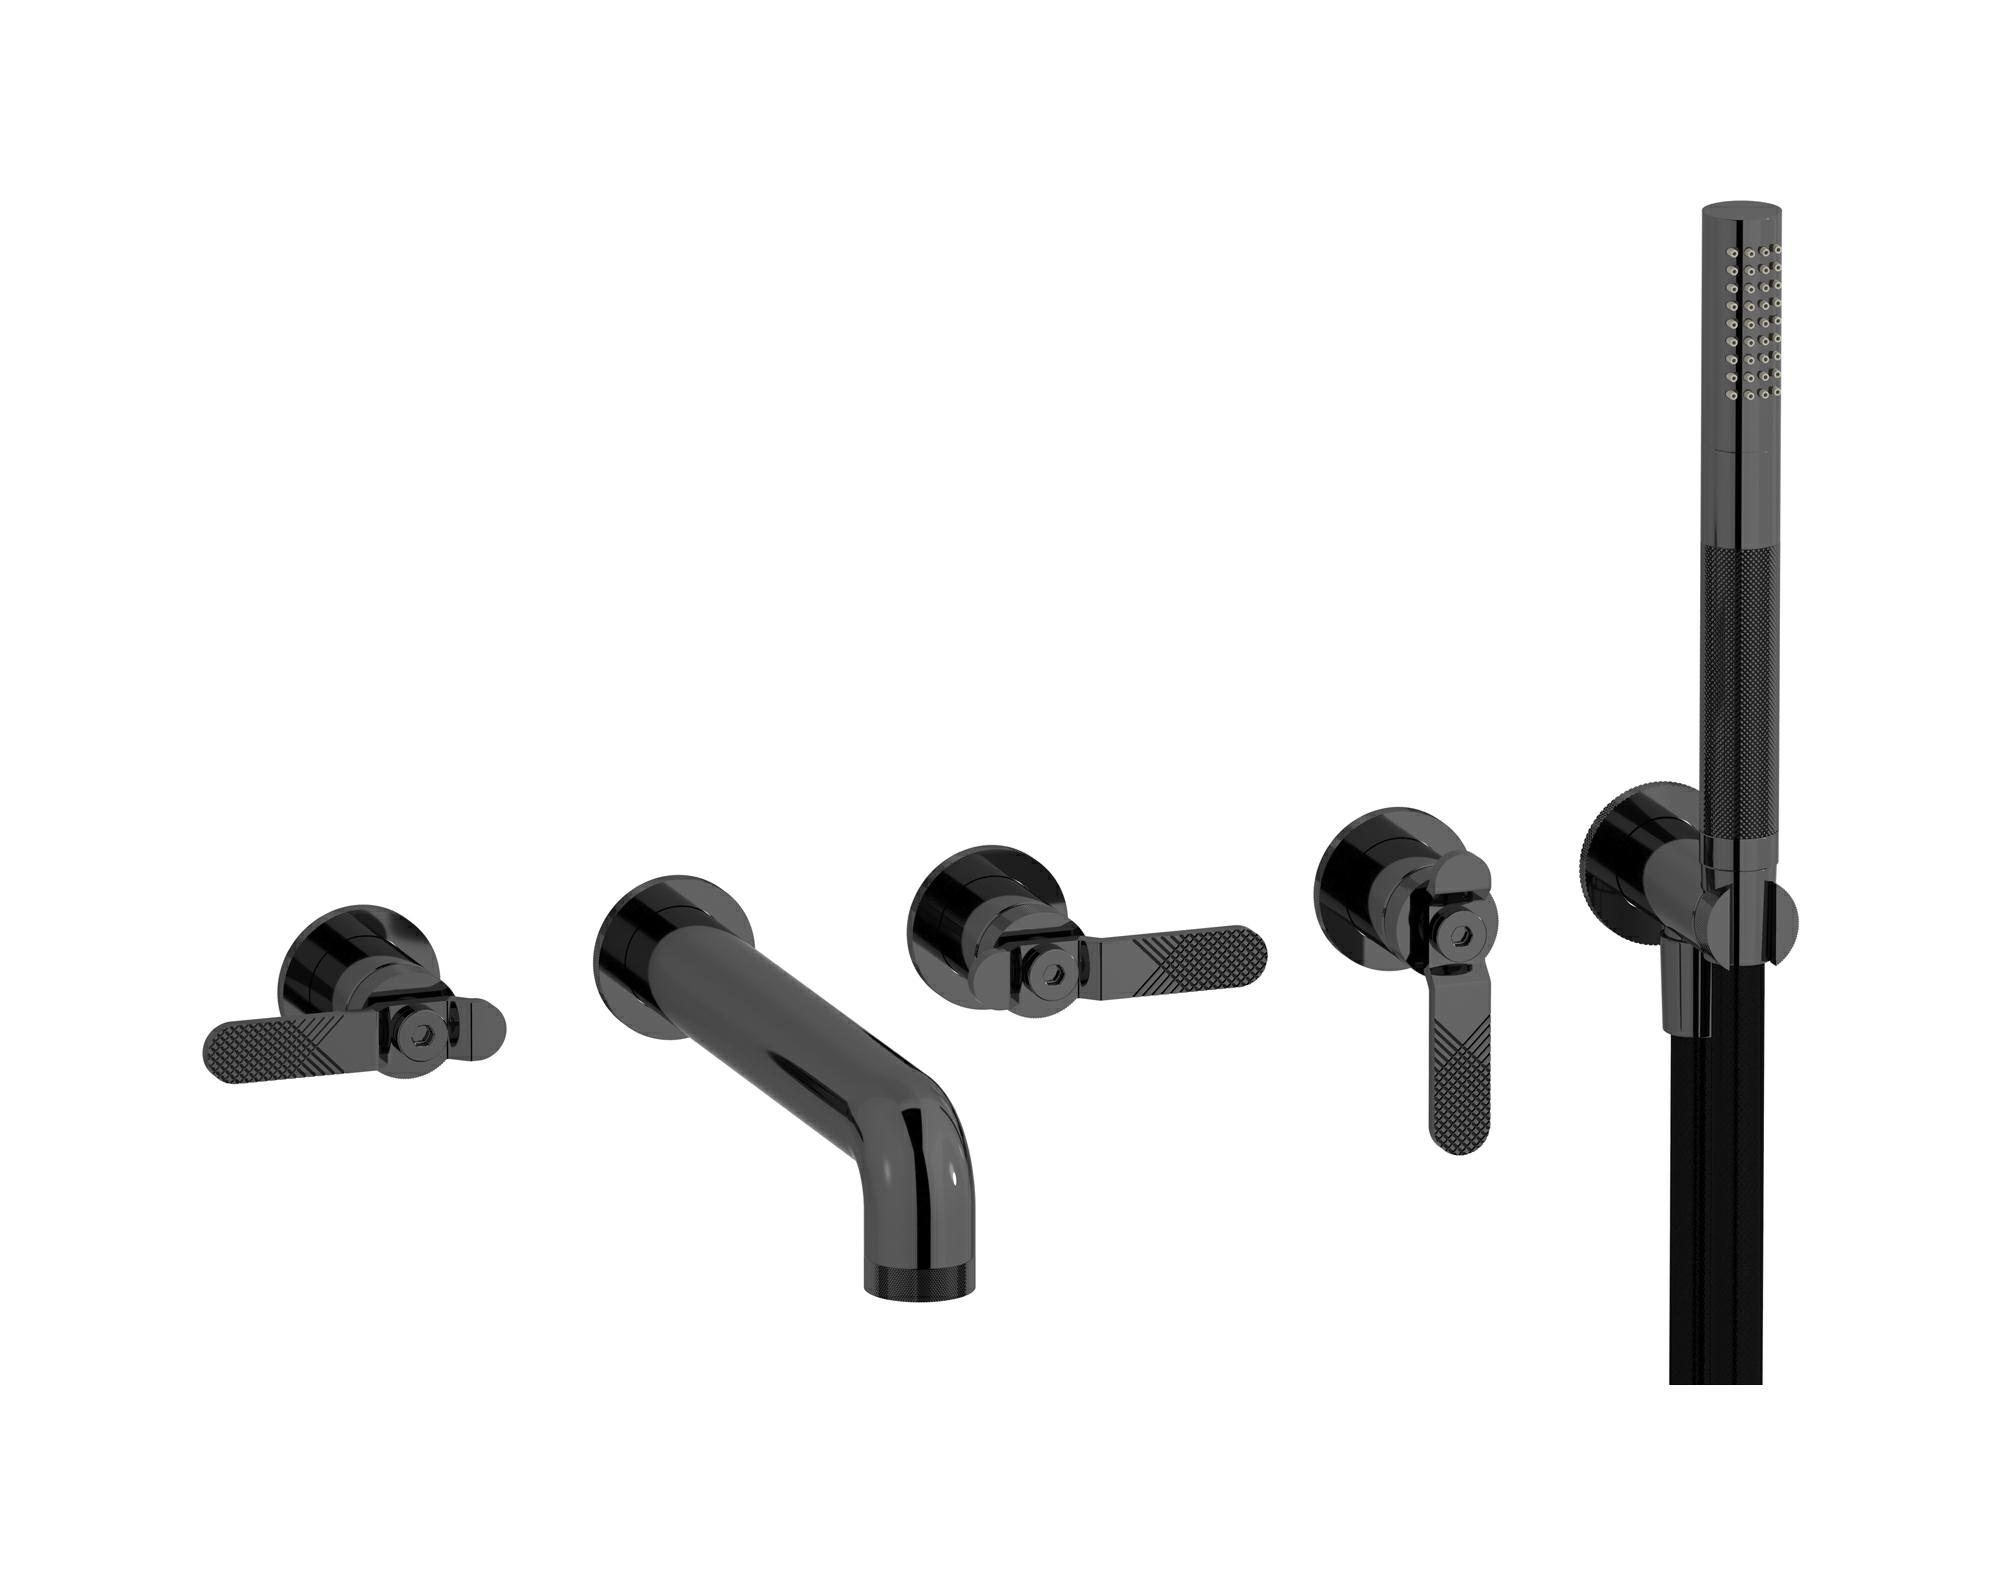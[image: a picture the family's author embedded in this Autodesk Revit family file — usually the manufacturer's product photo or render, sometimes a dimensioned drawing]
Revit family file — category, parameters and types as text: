
# Revit family: B2398
name_source: partatom
category: Apparecchi idraulici
units: mm (PartAtom-declared; Revit-internal decimal feet)

## family parameters
Basato su piano di lavoro = No
Condiviso = No
Mantieni orientamento annotazione = No
Numero OmniClass = 23.45.55.17
Punto di calcolo locali = No
Quota connettore circolare = Usa diametro
Sempre verticale = Sì
Taglio con vuoti quando caricato = No
Tipo di parte = Normale
Titolo OmniClass = Mixing Faucets

## types (13) — shared parameters
Cold water inlet = 10 mm  [stored 0.0328084 ft]
Commenti sul tipo = Five holes wall mounted bath filler with shower kit
Connessione CW = No
Connessione HW = No
Connessione di scarico = No
Connessione di ventilazione = No
Descrizione = Five holes wall mounted bath filler with shower kit
Hot water inlet = 10 mm  [stored 0.0328084 ft]
Produttore = IB Rubinetterie S.p.A.
URL = https://www.weareib.it
zero-valued in all types: Prospetto di default

## per-type parameters (varying)
| type | Finishes surface | Immagine tipo | Modello |
| Chrome | IB_Chrome | B2398CC.jpg | B2398CC |
| Black Chrome | IB_Black chrome | B2398CF.jpg | B2398CF |
| Brushed Black Chrome | IB_Brushed black chrome | B2398CS.jpg | B2398CS |
| Pale Gold | IB_Pale gold | B2398II.jpg | B2398II |
| Brushed Pale Gold | IB_brushed pale gold | B2398IS.jpg | B2398IS |
| Matt Black | IB_matt black | B2398NP.jpg | B2398NP |
| Natural Brass | IB_Brass | B2398ON.jpg | B2398ON |
| Gold | IB_gold | B2398OO.jpg | B2398OO |
| Brushed Gold | IB_brushed gold | B2398OS.jpg | B2398OS |
| Rose Gold | IB_Rose gold | B2398RS.jpg | B2398RS |
| Brushed Rose Gold | IB_Brushed rose gold | B2398SR.jpg | B2398SR |
| Brushed Nickel | IB_Brushed nickel | B2398SS.jpg | B2398SS |
| Modern Bronze | IB_Modern bronze | B2398MB.jpg | B2398MB |

note: [stored X ft] marks values corroborated as IEEE doubles in the binary element streams (Revit-internal decimal feet)
